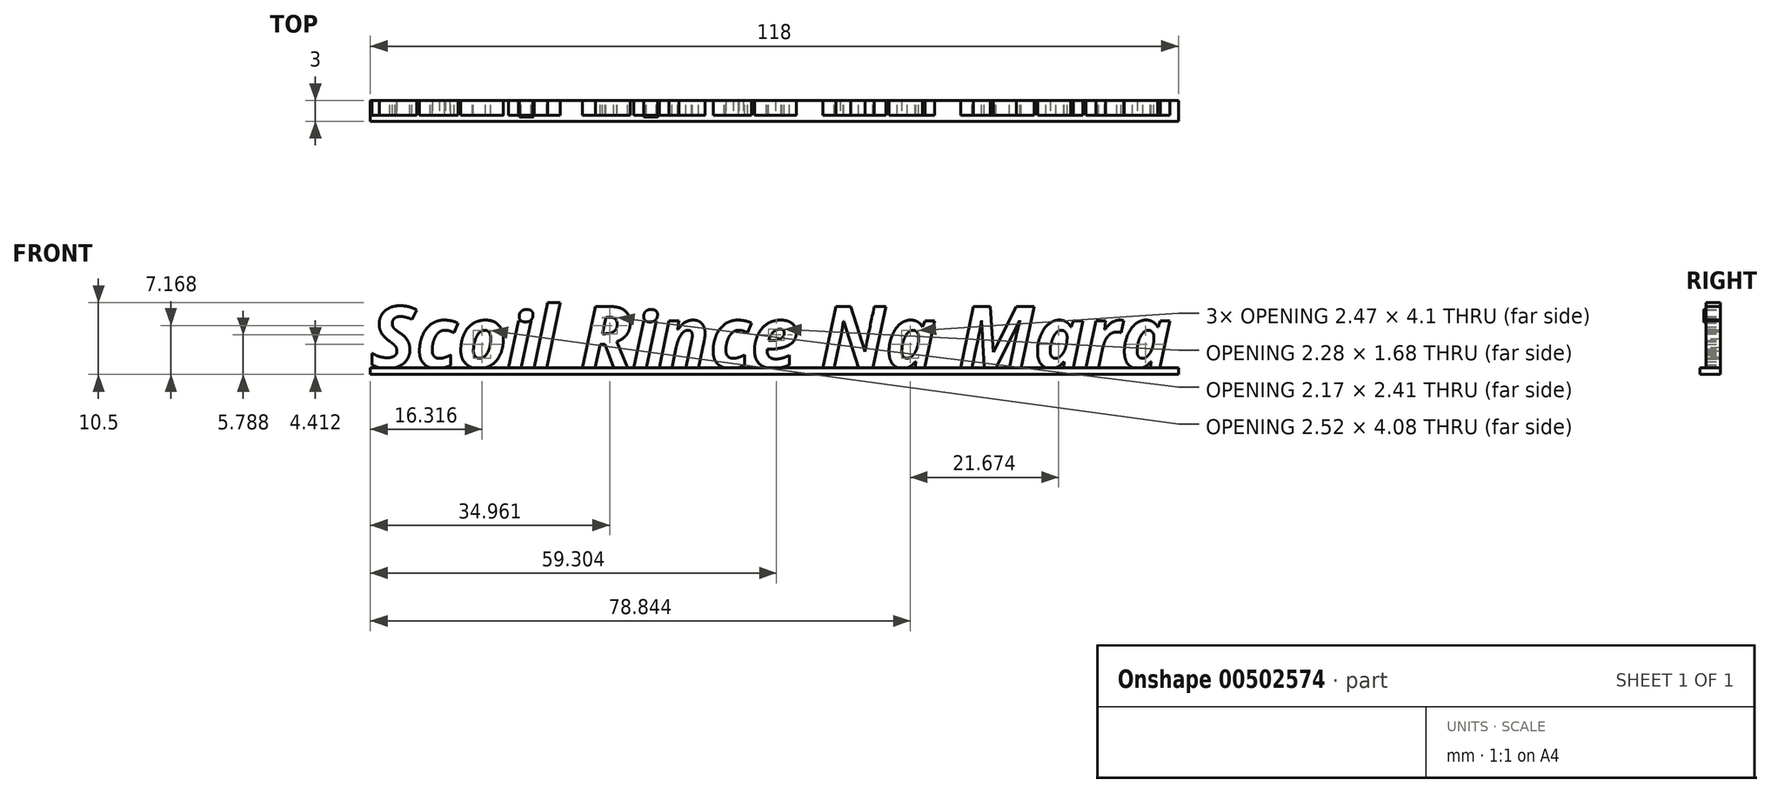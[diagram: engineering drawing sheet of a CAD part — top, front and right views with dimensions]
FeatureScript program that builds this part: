
annotation { "Feature Type Name" : "Feature", "Feature Type Description" : "" }
export const myFeature = defineFeature(function(context is Context, id is Id, definition is map)
    precondition{}
    {
        {
            var Q0;
            Q0=qCreatedBy(makeId("Front.planeOp"),FACE);
            var sketch = newSketch(context, id + "F0", { "sketchPlane" : qUnion([Q0])});
            skText(sketch, "E0", { "text": "Scoil Rince Na Mara", "fontName": "OpenSans-BoldItalic.ttf"});
            const initialGuessF0  = {"E0": [0, 0, 1, 0, 0.009]};
            skSetInitialGuess(sketch, initialGuessF0);
            skSolve(sketch);
        }
        {
            var Q0;
            Q0=qCreatedBy(makeId("Front.planeOp"),FACE);
            var sketch = newSketch(context, id + "F1", { "sketchPlane" : qUnion([Q0])});
            skLineSegment(sketch, "E1.bottom", {"start": v(0, 0) * mm, "end": v(118, 0) * mm});
            skLineSegment(sketch, "E1.top", {"start": v(0, -1) * mm, "end": v(118, -1) * mm});
            skLineSegment(sketch, "E1.left", {"start": v(0, 0) * mm, "end": v(0, -1) * mm});
            skLineSegment(sketch, "E1.right", {"start": v(118, 0) * mm, "end": v(118, -1) * mm});
            skSolve(sketch);
        }
        {
            var Q0;
            Q0=makeQuery(id+"F1.imprint","IMPRINT",FACE,{"disambiguationData":[TD([[makeQuery(id+"F1.imprint","IMPRINT",EDGE,{"derivedFrom":sQuery(id+"F1.wireOp",EDGE,"E1.bottom")}),-1.0]])]});
            extrude(context, id + "F2", {"entities" : qUnion([Q0]), "depth" : 3 * mm, "offsetDistance" : 25 * mm});
        }
        {
            var Q0;
            Q0 = qSketchRegion(id + "F0", true);
            extrude(context, id + "F3", {"entities" : qUnion([Q0]), "operationType" : NewBodyOperationType.ADD, "depth" : 2.1 * mm, "offsetDistance" : 25 * mm});
        }
        {
            var Q0;
            Q0=makeQuery(id+"F3.opExtrude","SWEPT_BODY",BODY,{"disambiguationData":[OSD([sQuery(id+"F0.wireOp",EDGE,"E0.sketch_text.stroke-60"),sQuery(id+"F0.wireOp",EDGE,"E0.sketch_text.stroke-61"),sQuery(id+"F0.wireOp",EDGE,"E0.sketch_text.stroke-62"),sQuery(id+"F0.wireOp",EDGE,"E0.sketch_text.stroke-63"),sQuery(id+"F0.wireOp",EDGE,"E0.sketch_text.stroke-64"),sQuery(id+"F0.wireOp",EDGE,"E0.sketch_text.stroke-65"),sQuery(id+"F0.wireOp",EDGE,"E0.sketch_text.stroke-66")])]});
            transform(context, id + "F4", {"entities" : qUnion([Q0]), "transformType" : TransformType.TRANSLATION_3D, "dx" : -0.2 * mm, "dy" : 0 * mm, "dz" : -1 * mm, "makeCopy" : false});
        }
        {
            var Q0;
            Q0=makeQuery(id+"F3.opExtrude","CAP_FACE",FACE,{"disambiguationData":[OSD([sQuery(id+"F0.wireOp",EDGE,"E0.sketch_text.stroke-60"),sQuery(id+"F0.wireOp",EDGE,"E0.sketch_text.stroke-61"),sQuery(id+"F0.wireOp",EDGE,"E0.sketch_text.stroke-62"),sQuery(id+"F0.wireOp",EDGE,"E0.sketch_text.stroke-63"),sQuery(id+"F0.wireOp",EDGE,"E0.sketch_text.stroke-64"),sQuery(id+"F0.wireOp",EDGE,"E0.sketch_text.stroke-65"),sQuery(id+"F0.wireOp",EDGE,"E0.sketch_text.stroke-66")])],"isStart":false});
            extrude(context, id + "F5", {"entities" : qUnion([Q0]), "depth" : 0.3 * mm, "offsetDistance" : 25 * mm});
        }
        {
            var Q0;
            Q0=makeQuery(id+"F3.opExtrude","SWEPT_BODY",BODY,{"disambiguationData":[OSD([sQuery(id+"F0.wireOp",EDGE,"E0.sketch_text.stroke-94"),sQuery(id+"F0.wireOp",EDGE,"E0.sketch_text.stroke-95"),sQuery(id+"F0.wireOp",EDGE,"E0.sketch_text.stroke-96"),sQuery(id+"F0.wireOp",EDGE,"E0.sketch_text.stroke-97"),sQuery(id+"F0.wireOp",EDGE,"E0.sketch_text.stroke-98"),sQuery(id+"F0.wireOp",EDGE,"E0.sketch_text.stroke-99"),sQuery(id+"F0.wireOp",EDGE,"E0.sketch_text.stroke-100")])]});
            transform(context, id + "F6", {"entities" : qUnion([Q0]), "transformType" : TransformType.TRANSLATION_3D, "dx" : -0.3 * mm, "dy" : 0 * mm, "dz" : -1 * mm, "makeCopy" : false});
        }
        {
            var Q0;
            Q0=makeQuery(id+"F3.opExtrude","CAP_FACE",FACE,{"disambiguationData":[OSD([sQuery(id+"F0.wireOp",EDGE,"E0.sketch_text.stroke-94"),sQuery(id+"F0.wireOp",EDGE,"E0.sketch_text.stroke-95"),sQuery(id+"F0.wireOp",EDGE,"E0.sketch_text.stroke-96"),sQuery(id+"F0.wireOp",EDGE,"E0.sketch_text.stroke-97"),sQuery(id+"F0.wireOp",EDGE,"E0.sketch_text.stroke-98"),sQuery(id+"F0.wireOp",EDGE,"E0.sketch_text.stroke-99"),sQuery(id+"F0.wireOp",EDGE,"E0.sketch_text.stroke-100")])],"isStart":false});
            extrude(context, id + "F7", {"entities" : qUnion([Q0]), "depth" : 0.3 * mm, "offsetDistance" : 25 * mm});
        }
    });
